# Revit family: Access_Door-Cabinet-Cendrex-Box-BTA
name_source: partatom
category: Specialty Equipment
revit_build: Autodesk Revit Architecture 2013 (Build: 20130531_2115(x64)
units: mm (PartAtom-declared; Revit-internal decimal feet)

## types (4) — shared parameters
Assembly Code = C1020700
Available Options = http://cendrex.com
Cendrex LEED Ready Program = http://www.cendrex.com
Construction Material = Metal - Cendrex - Aluminum
Default Elevation = 0"
Description = Cabinets and Valve Boxes
Finish = Metal - Cendrex - Powder Coated White
Manufacturer = Cendrex
Max Area = 900 in²
Model = BTA
Product Documentation Link = http://cendrex.com
Product Page URL = http://cendrex.com
URL = http://www.cendrex.com

## per-type parameters (varying)
| type | 4in Frame Depth | 6in Frame Depth | Area | Door Height | Door Width | Frame Depth | Frame Height | Frame Width | Height Calc | Width Calc |
| Custom | Yes | No | 750 in² | 30" | 25" | 4" | 29 1/8" | 24 1/8" | 30" | 25" |
| 81/4 x 8 1/4 | No | Yes | 68.06 in² | 8 1/4" | 8 1/4" | 6" | 7 3/8" | 7 3/8" | 8 1/4" | 8 1/4" |
| 12 x 12 | No | Yes | 144 in² | 12" | 12" | 6" | 11 1/8" | 11 1/8" | 12" | 12" |
| 16 x 16 | Yes | No | 256 in² | 16" | 16" | 4" | 15 1/8" | 15 1/8" | 16" | 16" |

## geometry (parser evidence)
native form markers: Blend x17, Sweep x7
no freeform markers — native parametric forms only
